# Revit family: CENTUM IB-Anbindung
name_source: partatom
category: HLS-Bauteile
revit_build: Autodesk Revit 2017 (Build: 20190508_0315(x64)
units: mm (PartAtom-declared; Revit-internal decimal feet)

## family parameters
Arbeitsebenenbasiert = Ja
Beim Laden mit Abzugskörper schneiden = Nein
Bemaßung runder Anschluss = Durchmesser verwenden
Gemeinsam genutzt = Ja
Immer vertikal = Nein
Raumberechnungspunkt = Nein
Teiletyp = Normal

## types (2) — shared parameters
Fabrikat = MEFA
Firma = MEFA Befestigungs- und Montagesysteme GmbH
Gewinde = M12
Gewindestifttyp = M12 x 35
Hammerschraubentyp = M12 x 35
Kurztext1 = IB-Anbindung CENTUM
Lieferumfang = Hammerkopfschraube, Hutprofil, 6-kt.-Mutter
Material = Stahl
Materialname = S235
Mengeneinheit = St
Oberflaeche = Zink-Nickel
Profiltyp = XL 100, XL 120, XL 200
Vorgabe-Ansicht = 1219 mm
max. zul. Last = 2.00 kN
vpe = 1 St

## per-type parameters (varying)
| type | Artikelnummer | Baulänge | EAN | Gewicht | Gewicht pro Bauteil | Gewindestift | Kurztext2 | für Profilhöhe | x |
| CENTUM IB- Anbindung 40-45 | 1640017040 | 70 mm | 4250928436931 | 0.17 kg | 0.17 kg | Gewindestifte für Centum IB : Gewindestift M12x35für Centum IB | für Profilhöhe 40 - 45 mm | 40 - 45 mm | 13 mm |
| CENTUM IB- Anbindung 60 | 1640017060 | 90 mm | 4250928436948 | 0.18 kg | 0.18 kg | Gewindestifte für Centum IB : Gewindestift M12x50für Centum IB | für Profilhöhe 60 mm | 60 mm | 27 mm  [stored 0.0885827 ft] |

note: [stored X ft] marks values corroborated as IEEE doubles in the binary element streams (Revit-internal decimal feet)

## geometry (parser evidence)
native form markers: Sweep x3
no freeform markers — native parametric forms only
